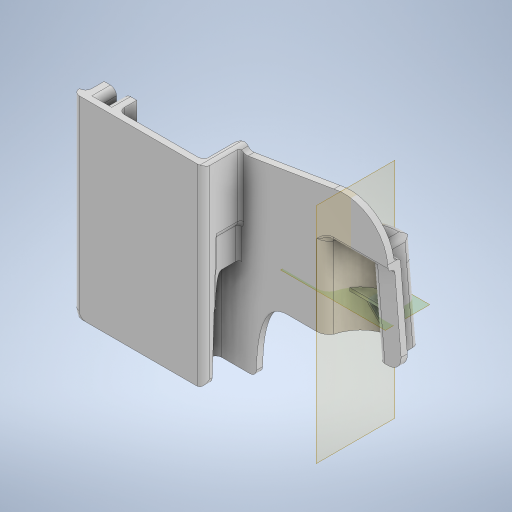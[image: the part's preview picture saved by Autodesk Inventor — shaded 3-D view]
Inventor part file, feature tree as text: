
AUTODESK INVENTOR PART (.ipt)
format: ipt  version: 2023 (Build 270158000, 158)  size: 859,136 bytes
history: native  units: in
note: dims shown in document units (in); Inventor stores cm internally (conversion verified against a paired STEP export)
features: sketch x19, extrude x18, fillet x13, projected_geometry x8, sweep x2, plane x2
ambient origin geometry x8: Origin, YZ Plane, XZ Plane, XY Plane, X Axis, Y Axis, Z Axis, Center Point
bodies: Solid1 (feature_tree)
feature tree (62):
  extrude  "Extrusion1"  Depth=0.1in
  extrude  "Extrusion2"  Depth=0.125in
  extrude  "Extrusion3"  Depth=0.0312in TaperAngle=0.0deg
  sketch  "Sketch4"  dims[d38=0.0625in d39=0.0312in d40=0.0in]
  extrude  "Extrusion8"  Depth=0.5in
  extrude  "Extrusion9"  Depth=0.4375in
  sketch  "Sketch9"  dims[d51=0.375in d52=0.4375in]
  sweep  "Sweep1"
  extrude  "Extrusion12"  TaperAngle=0.0deg  [1 undecoded]
  extrude  "Extrusion14"  Depth=0.05in
  fillet  "Fillet11"  Radius=1.63in
  fillet  "Fillet12"  Radius=0.1in
  fillet  "Fillet13"  Radius=0.1in
  fillet  "Fillet14"  Radius=0.05in
  fillet  "Fillet15"  Radius=0.05in
  extrude  "Extrusion17"  Depth=0.1in TaperAngle=0.0deg
  extrude  "Extrusion18"  Depth=0.1in
  extrude  "Extrusion21"  TaperAngle=0.0deg  [1 undecoded]
  sketch  "Sketch33"  dims[d96=0.1in d103=0.1in d104=0.0in]
  sweep  "Sweep4"
  extrude  "Extrusion22"  Depth=1.5in
  extrude  "Extrusion24"  Depth=0.1in
  extrude  "Extrusion25"  Depth=0.1in
  fillet  "Fillet41"  Radius=0.1in
  fillet  "Fillet42"  Radius=0.7in
  fillet  "Fillet43"  Radius=0.2in
  fillet  "Fillet44"  Radius=0.1in
  fillet  "Fillet46"  Radius=0.05in
  fillet  "Fillet47"  Radius=0.1in
  plane  "Work Plane9"
  extrude  "Extrusion26"  Depth=0.1in
  plane  "Work Plane10"
  extrude  "Extrusion27"  [1 undecoded]
  extrude  "Extrusion28"  Depth=0.1in
  extrude  "Extrusion30"  Depth=0.05in TaperAngle=0.0deg
  extrude  "Extrusion31"  Depth=0.05in TaperAngle=0.0deg
  fillet  "Fillet55"  Radius=2.2in
  fillet  "Fillet57"  Radius=0.1in
  sketch  "Sketch1"  dims[d0=3.0in d1=0.25in d2=2.5in d3=1.75in d5=1.125in d6=2.125in d7=0.1in d8=0.0in]
  sketch  "Sketch2"  dims[d9=0.5in d10=1.0in d11=0.125in d12=0.0625in d13=0.125in d16=0.1in d17=0.0in d20=0.35in]
  sketch  "Sketch3"  dims[d21=0.6in d22=0.0in d23=0.125in d24=1.0in]
  sketch  "Sketch8"  dims[d41=1.0in d42=0.0625in d43=0.375in d44=0.0in d50=0.5in]
  sketch  "3D Sketch1"
  sketch  "Sketch23"  dims[d53=0.1in d55=0.1in]
  sketch  "Sketch27"  dims[d57=0.1in d66=0.0in d67=0.0in]
  sketch  "Sketch28"  dims[d72=1.5in d73=0.0in d87=0.05in d88=1.63in d89=0.0in d92=0.1in d93=0.1in d94=0.05in d95=0.05in]
  projected_geometry  "Projected Loop5"
  projected_geometry  "Projected Loop6"
  sketch  "3D Sketch8"
  sketch  "Sketch36"  dims[d106=0.1in d107=0.0in d114=0.28in]
  projected_geometry  "Projected Loop9"
  sketch  "Sketch37"  dims[d123=0.1in d124=0.0in d125=0.0in d126=0.0in]
  projected_geometry  "Projected Loop11"
  sketch  "Sketch38"  dims[d127=1.4in d128=0.0in d129=0.38in]
  projected_geometry  "Projected Loop12"
  projected_geometry  "Projected Loop13"
  projected_geometry  "Projected Loop14"
  sketch  "Sketch39"  dims[d134=3.2875in d135=0.0in d151=1.5in]
  sketch  "Sketch41"  dims[d156=1.85in d157=0.0in d158=0.1in]
  sketch  "Sketch43"  dims[d160=0.6in d162=0.1in d163=0.1in d164=0.7in d165=0.2in d166=0.1in d167=0.05in d168=0.1in]
  projected_geometry  "Projected Loop15"
  sketch  "Sketch44"  dims[d170=0.2625in d171=0.102in d173=-0.6in d174=0.18in d175=0.05in d176=0.0in d177=0.05in d178=0.0in d180=2.2in d181=0.0in d183=0.1in d184=3.1in d195=0.3in d196=0.0in d197=0.4in d198=0.125in d200=2.9in d201=0.0in d207=0.2in d208=0.06in d209=0.1in d211=0.1in d212=0.525in d18=0.5in d19=0.0344in d33=0.5in d34=0.0344in d35=0.5in d36=0.0344in d37=0.5in d54=0.5in d56=0.5in d58=0.5in d59=0.0344in d68=0.5in d69=0.0344in d70=0.5in d71=0.0344in d76=0.5in d77=0.0344in d78=0.5in d79=0.0344in d80=0.0in d81=0.0in d82=0.5in d83=0.0344in d84=0.5in d85=0.0344in d86=0.0in d90=0.0in d91=0.0344in d97=0.0in d98=0.0in d99=0.0in d105=0.5in d108=0.0in d109=0.0in d110=0.0in d111=0.0in d112=0.0in d113=0.0in d140=0.0in d141=0.0in d142=0.0in d143=0.0in d147=0.0in d148=0.0in d149=0.0in d150=0.0in d154=0.0in d155=0.0in d172=0.0in d193=0.0in d194=0.0in d203=0.0in d204=0.0in d205=0.0in d206=0.0in d210=0.0in d213=0.0in d214=0.0in d215=0.0in d216=0.0in]
note: 3 required parameter values undecoded (feature->parameter linkage not recoverable at this tier; creation-order binding heuristic only, values carry confidence <= 0.55)
